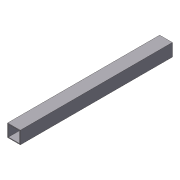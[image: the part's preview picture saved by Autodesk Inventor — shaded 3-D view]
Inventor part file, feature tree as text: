
AUTODESK INVENTOR PART (.ipt)
format: ipt  version: 2012 (Build 160160000, 160)  size: 71,168 bytes
history: native  units: in
note: dims shown in document units (in); Inventor stores cm internally (conversion verified against a paired STEP export)
features: extrude x1, shell x1, sketch x1
ambient origin geometry x8: Origin, YZ Plane, XZ Plane, XY Plane, X Axis, Y Axis, Z Axis, Center Point
bodies: Solid1 (feature_tree)
feature tree (3):
  extrude  "Extrusion1"  Depth=1.0in
  shell  "Shell1"  Thickness=12.0in
  sketch  "Sketch1"  dims[d0=1.0in d1=1.0in d2=12.0in d3=0.0in d4=0.0625in]
